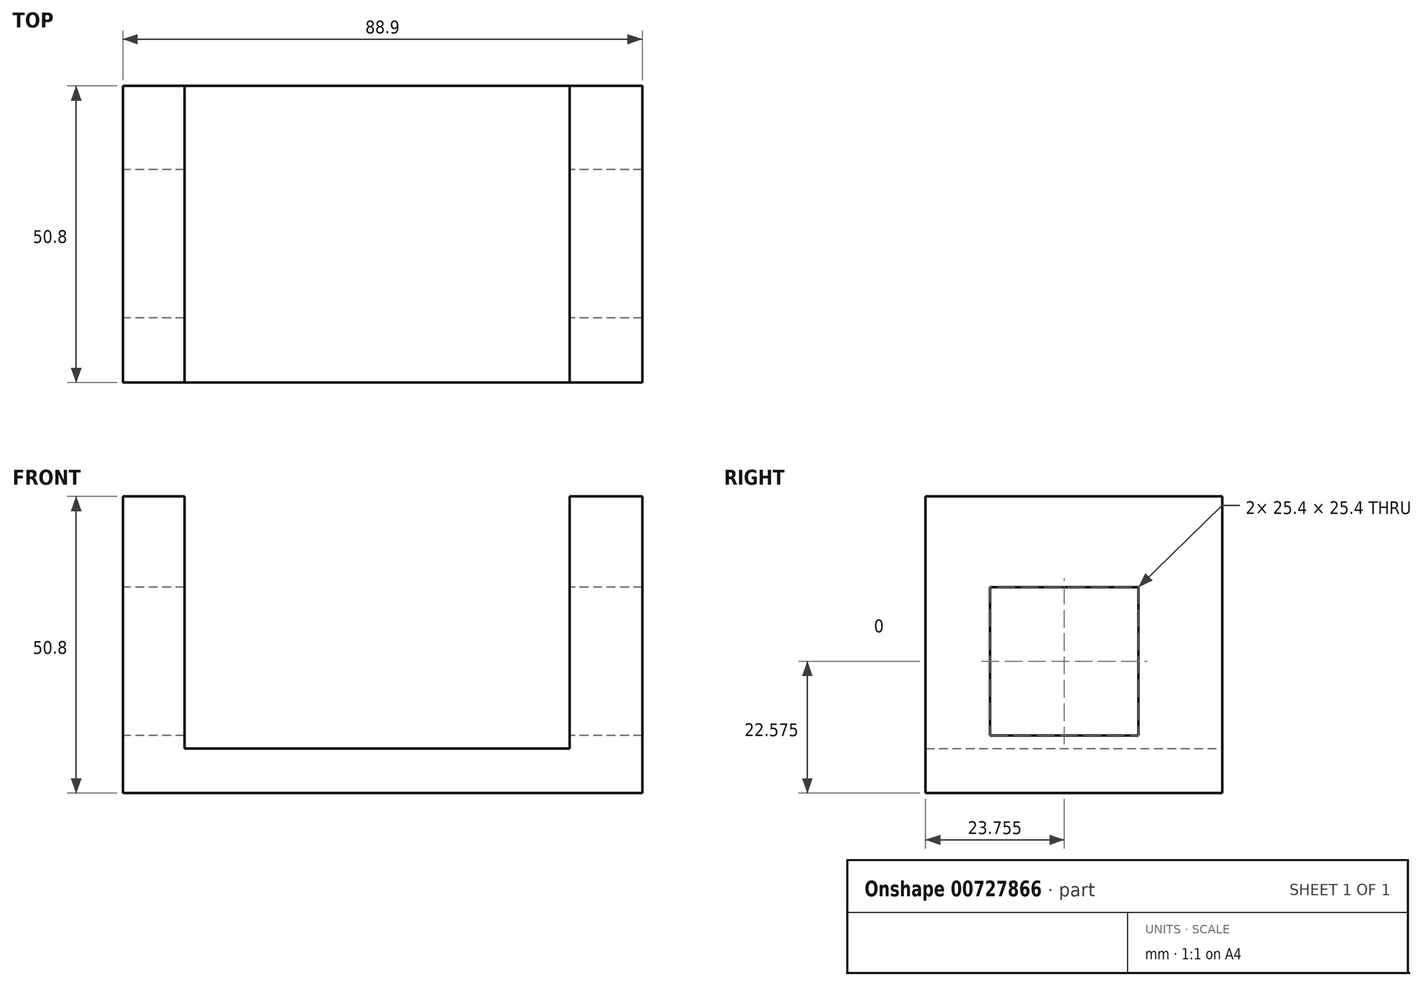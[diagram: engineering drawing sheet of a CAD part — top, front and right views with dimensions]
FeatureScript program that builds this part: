
annotation { "Feature Type Name" : "Feature", "Feature Type Description" : "" }
export const myFeature = defineFeature(function(context is Context, id is Id, definition is map)
    precondition{}
    {
        {
            var Q0;
            Q0=qCreatedBy(makeId("Right.planeOp"),FACE);
            var sketch = newSketch(context, id + "F0", { "sketchPlane" : qUnion([Q0])});
            skLineSegment(sketch, "E0.bottom", {"start": v(-17.03, 22.35) * mm, "end": v(33.77, 22.35) * mm});
            skLineSegment(sketch, "E0.top", {"start": v(-17.03, -28.45) * mm, "end": v(33.77, -28.45) * mm});
            skLineSegment(sketch, "E0.left", {"start": v(-17.03, 22.35) * mm, "end": v(-17.03, -28.45) * mm});
            skLineSegment(sketch, "E0.right", {"start": v(33.77, 22.35) * mm, "end": v(33.77, -28.45) * mm});
            skLineSegment(sketch, "E1.bottom", {"start": v(-5.97, 6.82) * mm, "end": v(19.43, 6.82) * mm});
            skLineSegment(sketch, "E1.top", {"start": v(-5.97, -18.58) * mm, "end": v(19.43, -18.58) * mm});
            skLineSegment(sketch, "E1.left", {"start": v(-5.97, 6.82) * mm, "end": v(-5.97, -18.58) * mm});
            skLineSegment(sketch, "E1.right", {"start": v(19.43, 6.82) * mm, "end": v(19.43, -18.58) * mm});
            skSolve(sketch);
        }
        {
            var Q0;
            Q0=makeQuery(id+"F0.imprint","IMPRINT",FACE,{"disambiguationData":[TD([[makeQuery(id+"F0.imprint","IMPRINT",EDGE,{"derivedFrom":sQuery(id+"F0.wireOp",EDGE,"E0.bottom")}),-1.0]])]});
            extrude(context, id + "F1", {"entities" : qUnion([Q0]), "depth" : 88.9 * mm, "offsetDistance" : 25.4 * mm});
        }
        {
            var Q0;
            Q0=makeQuery(id+"F1.opExtrude","SWEPT_FACE",FACE,{"disambiguationData":[OSD([sQuery(id+"F0.wireOp",EDGE,"E0.right")])]});
            var sketch = newSketch(context, id + "F2", { "sketchPlane" : qUnion([Q0])});
            skLineSegment(sketch, "E2.bottom", {"start": v(-76.45, 22.35) * mm, "end": v(-10.55, 22.35) * mm});
            skLineSegment(sketch, "E2.top", {"start": v(-76.45, -20.83) * mm, "end": v(-10.55, -20.83) * mm});
            skLineSegment(sketch, "E2.left", {"start": v(-76.45, 22.35) * mm, "end": v(-76.45, -20.83) * mm});
            skLineSegment(sketch, "E2.right", {"start": v(-10.55, 22.35) * mm, "end": v(-10.55, -20.83) * mm});
            skSolve(sketch);
        }
        {
            var Q0;
            Q0=makeQuery(id+"F2.imprint","IMPRINT",FACE,{"disambiguationData":[TD([[makeQuery(id+"F2.imprint","IMPRINT",EDGE,{"derivedFrom":sQuery(id+"F2.wireOp",EDGE,"E2.bottom")}),-1.0]])]});
            extrude(context, id + "F3", {"entities" : qUnion([Q0]), "operationType" : NewBodyOperationType.REMOVE, "oppositeDirection" : true, "depth" : 50.8 * mm, "offsetDistance" : 25.4 * mm});
        }
    });
